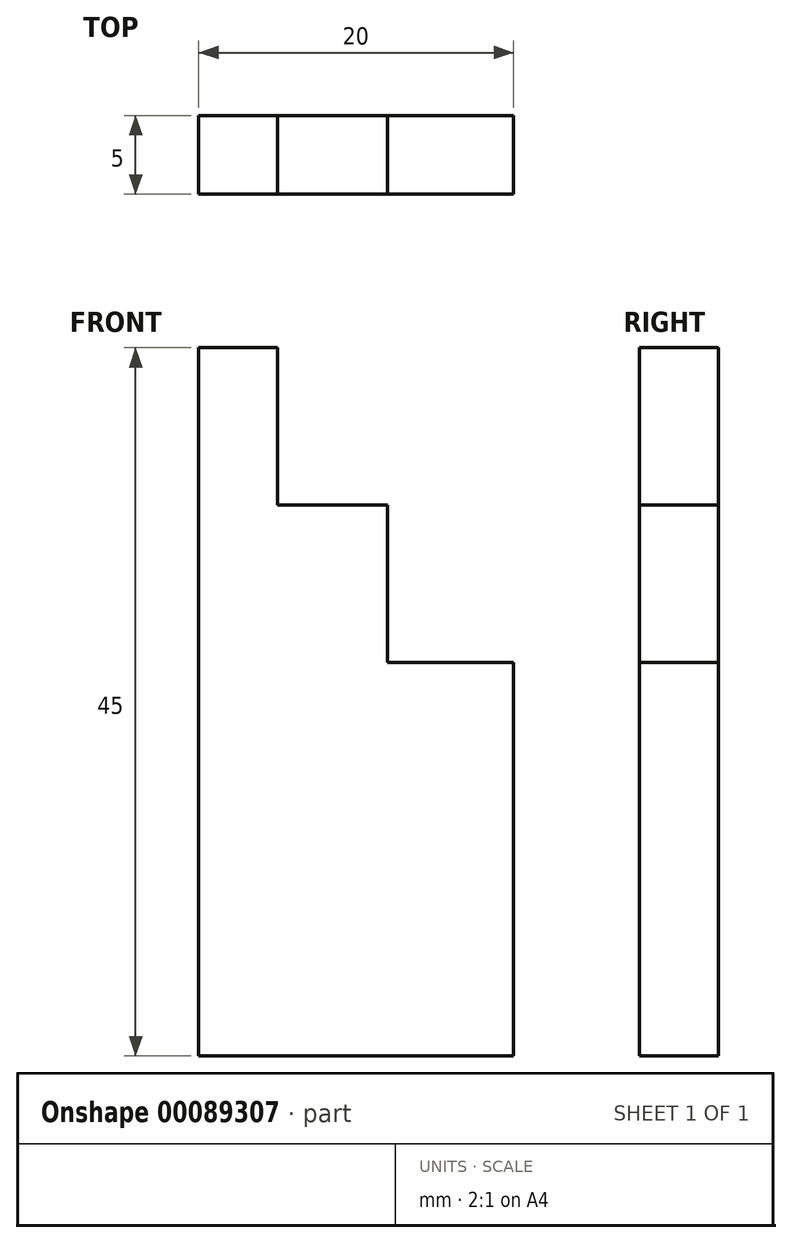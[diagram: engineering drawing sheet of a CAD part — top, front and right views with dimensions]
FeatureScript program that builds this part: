
annotation { "Feature Type Name" : "Feature", "Feature Type Description" : "" }
export const myFeature = defineFeature(function(context is Context, id is Id, definition is map)
    precondition{}
    {
        {
            var Q0;
            Q0=qCreatedBy(makeId("Front.planeOp"),FACE);
            var sketch = newSketch(context, id + "F0", { "sketchPlane" : qUnion([Q0])});
            skLineSegment(sketch, "E0", {"start": v(0, 0) * mm, "end": v(0, 45) * mm});
            skLineSegment(sketch, "E1", {"start": v(0, 45) * mm, "end": v(5, 45) * mm});
            skLineSegment(sketch, "E2", {"start": v(5, 45) * mm, "end": v(5, 35) * mm});
            skLineSegment(sketch, "E3", {"start": v(5, 35) * mm, "end": v(12, 35) * mm});
            skLineSegment(sketch, "E4", {"start": v(12, 35) * mm, "end": v(12, 25) * mm});
            skLineSegment(sketch, "E5", {"start": v(12, 25) * mm, "end": v(20, 25) * mm});
            skLineSegment(sketch, "E6", {"start": v(20, 25) * mm, "end": v(20, 0) * mm});
            skLineSegment(sketch, "E7", {"start": v(20, 0) * mm, "end": v(0, 0) * mm});
            skSolve(sketch);
        }
        {
            var Q0;
            Q0=makeQuery(id+"F0.imprint","IMPRINT",FACE,{"disambiguationData":[TD([[makeQuery(id+"F0.imprint","IMPRINT",EDGE,{"derivedFrom":sQuery(id+"F0.wireOp",EDGE,"E0")}),-1.0]])]});
            extrude(context, id + "F1", {"entities" : qUnion([Q0]), "depth" : 5 * mm});
        }
    });
